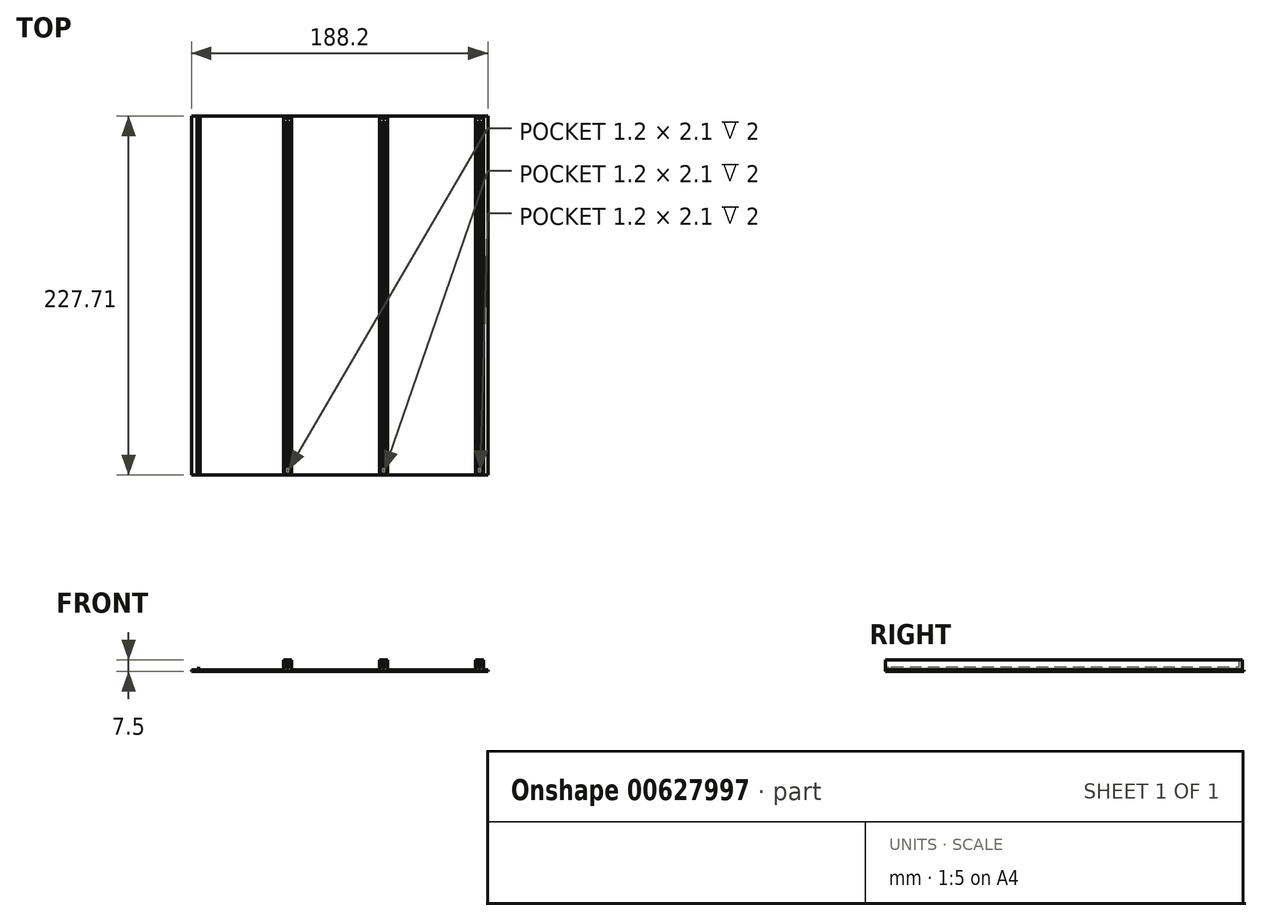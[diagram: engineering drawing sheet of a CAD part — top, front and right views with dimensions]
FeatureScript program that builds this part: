
annotation { "Feature Type Name" : "Feature", "Feature Type Description" : "" }
export const myFeature = defineFeature(function(context is Context, id is Id, definition is map)
    precondition{}
    {
        {
            var Q0;
            Q0=qCreatedBy(makeId("Top.planeOp"),FACE);
            var sketch = newSketch(context, id + "F0", { "sketchPlane" : qUnion([Q0])});
            skLineSegment(sketch, "E0.bottom", {"start": v(0, 0) * mm, "end": v(5.2, 0) * mm});
            skLineSegment(sketch, "E0.top", {"start": v(0, 226.71) * mm, "end": v(5.2, 226.71) * mm});
            skLineSegment(sketch, "E0.left", {"start": v(0, 0) * mm, "end": v(0, 226.71) * mm});
            skLineSegment(sketch, "E0.right", {"start": v(5.2, 0) * mm, "end": v(5.2, 226.71) * mm});
            skLineSegment(sketch, "E1.1.0.0", {"start": v(66.2, 0) * mm, "end": v(66.2, 226.71) * mm});
            skLineSegment(sketch, "E1.1.0.1", {"start": v(61, 0) * mm, "end": v(61, 226.71) * mm});
            skLineSegment(sketch, "E1.1.0.2", {"start": v(61, 226.71) * mm, "end": v(66.2, 226.71) * mm});
            skLineSegment(sketch, "E1.1.0.3", {"start": v(61, 0) * mm, "end": v(66.2, 0) * mm});
            skLineSegment(sketch, "E1.2.0.0", {"start": v(127.2, 0) * mm, "end": v(127.2, 226.71) * mm});
            skLineSegment(sketch, "E1.2.0.1", {"start": v(122, 0) * mm, "end": v(122, 226.71) * mm});
            skLineSegment(sketch, "E1.2.0.2", {"start": v(122, 226.71) * mm, "end": v(127.2, 226.71) * mm});
            skLineSegment(sketch, "E1.2.0.3", {"start": v(122, 0) * mm, "end": v(127.2, 0) * mm});
            skLineSegment(sketch, "E1.direction1", {"start": v(0, 0) * mm, "end": v(61, 0) * mm, "construction": true});
            skSolve(sketch);
        }
        {
            var Q0;
            Q0=makeQuery(id+"F0.imprint","IMPRINT",FACE,{"disambiguationData":[TD([[makeQuery(id+"F0.imprint","IMPRINT",EDGE,{"derivedFrom":sQuery(id+"F0.wireOp",EDGE,"E0.bottom")}),1.0]])]});
            var Q1;
            Q1=makeQuery(id+"F0.imprint","IMPRINT",FACE,{"disambiguationData":[TD([[makeQuery(id+"F0.imprint","IMPRINT",EDGE,{"derivedFrom":sQuery(id+"F0.wireOp",EDGE,"E1.1.0.0")}),1.0]])]});
            var Q2;
            Q2=makeQuery(id+"F0.imprint","IMPRINT",FACE,{"disambiguationData":[TD([[makeQuery(id+"F0.imprint","IMPRINT",EDGE,{"derivedFrom":sQuery(id+"F0.wireOp",EDGE,"E1.2.0.0")}),1.0]])]});
            extrude(context, id + "F1", {"entities" : qUnion([Q0, Q1, Q2]), "depth" : 2 * mm, "offsetDistance" : 25 * mm});
        }
        {
            var Q0;
            Q0=makeQuery(id+"F1.opExtrude","CAP_FACE",FACE,{"disambiguationData":[OSD([sQuery(id+"F0.wireOp",EDGE,"E0.bottom"),sQuery(id+"F0.wireOp",EDGE,"E0.top"),sQuery(id+"F0.wireOp",EDGE,"E0.left"),sQuery(id+"F0.wireOp",EDGE,"E0.right")])],"isStart":false});
            var sketch = newSketch(context, id + "F2", { "sketchPlane" : qUnion([Q0])});
            skLineSegment(sketch, "E2.bottom", {"start": v(0, 0) * mm, "end": v(2, 0) * mm});
            skLineSegment(sketch, "E2.top", {"start": v(0, 226.71) * mm, "end": v(5.2, 226.71) * mm});
            skLineSegment(sketch, "E2.left", {"start": v(0, 0) * mm, "end": v(0, 226.71) * mm});
            skLineSegment(sketch, "E2.right", {"start": v(5.2, 0) * mm, "end": v(5.2, 226.71) * mm});
            skLineSegment(sketch, "E3.top", {"start": v(2, 224.71) * mm, "end": v(3.2, 224.71) * mm});
            skLineSegment(sketch, "E3.left", {"start": v(2, 0) * mm, "end": v(2, 224.71) * mm});
            skLineSegment(sketch, "E3.right", {"start": v(3.2, 0) * mm, "end": v(3.2, 224.71) * mm});
            skLineSegment(sketch, "E4.trimOffspring", {"start": v(3.2, 0) * mm, "end": v(5.2, 0) * mm});
            skLineSegment(sketch, "E5.1.0.0", {"start": v(61, 0) * mm, "end": v(61, 226.71) * mm});
            skLineSegment(sketch, "E5.1.0.1", {"start": v(66.2, 0) * mm, "end": v(66.2, 226.71) * mm});
            skLineSegment(sketch, "E5.1.0.2", {"start": v(63, 0) * mm, "end": v(63, 224.71) * mm});
            skLineSegment(sketch, "E5.1.0.3", {"start": v(64.2, 0) * mm, "end": v(64.2, 224.71) * mm});
            skLineSegment(sketch, "E5.1.0.4", {"start": v(64.2, 0) * mm, "end": v(66.2, 0) * mm});
            skLineSegment(sketch, "E5.1.0.5", {"start": v(61, 226.71) * mm, "end": v(66.2, 226.71) * mm});
            skLineSegment(sketch, "E5.1.0.6", {"start": v(61, 0) * mm, "end": v(63, 0) * mm});
            skLineSegment(sketch, "E5.1.0.7", {"start": v(63, 224.71) * mm, "end": v(64.2, 224.71) * mm});
            skLineSegment(sketch, "E5.2.0.0", {"start": v(122, 0) * mm, "end": v(122, 226.71) * mm});
            skLineSegment(sketch, "E5.2.0.1", {"start": v(127.2, 0) * mm, "end": v(127.2, 226.71) * mm});
            skLineSegment(sketch, "E5.2.0.2", {"start": v(124, 0) * mm, "end": v(124, 224.71) * mm});
            skLineSegment(sketch, "E5.2.0.3", {"start": v(125.2, 0) * mm, "end": v(125.2, 224.71) * mm});
            skLineSegment(sketch, "E5.2.0.4", {"start": v(125.2, 0) * mm, "end": v(127.2, 0) * mm});
            skLineSegment(sketch, "E5.2.0.5", {"start": v(122, 226.71) * mm, "end": v(127.2, 226.71) * mm});
            skLineSegment(sketch, "E5.2.0.6", {"start": v(122, 0) * mm, "end": v(124, 0) * mm});
            skLineSegment(sketch, "E5.2.0.7", {"start": v(124, 224.71) * mm, "end": v(125.2, 224.71) * mm});
            skLineSegment(sketch, "E5.direction1", {"start": v(0, 0) * mm, "end": v(61, 0) * mm, "construction": true});
            skSolve(sketch);
        }
        {
            var Q0;
            Q0=makeQuery(id+"F2.imprint","IMPRINT",FACE,{"disambiguationData":[TD([[makeQuery(id+"F2.imprint","IMPRINT",EDGE,{"derivedFrom":sQuery(id+"F2.wireOp",EDGE,"E2.bottom")}),1.0]])]});
            var Q1;
            Q1=makeQuery(id+"F2.imprint","IMPRINT",FACE,{"disambiguationData":[TD([[makeQuery(id+"F2.imprint","IMPRINT",EDGE,{"derivedFrom":sQuery(id+"F2.wireOp",EDGE,"E5.1.0.0")}),-1.0]])]});
            var Q2;
            Q2=makeQuery(id+"F2.imprint","IMPRINT",FACE,{"disambiguationData":[TD([[makeQuery(id+"F2.imprint","IMPRINT",EDGE,{"derivedFrom":sQuery(id+"F2.wireOp",EDGE,"E5.2.0.0")}),-1.0]])]});
            extrude(context, id + "F3", {"entities" : qUnion([Q0, Q1, Q2]), "operationType" : NewBodyOperationType.ADD, "depth" : 4.5 * mm, "offsetDistance" : 25 * mm});
        }
        {
            var Q0;
            Q0=makeQuery(id+"F1.opExtrude","CAP_FACE",FACE,{"disambiguationData":[OSD([sQuery(id+"F0.wireOp",EDGE,"E0.bottom"),sQuery(id+"F0.wireOp",EDGE,"E0.top"),sQuery(id+"F0.wireOp",EDGE,"E0.left"),sQuery(id+"F0.wireOp",EDGE,"E0.right")])],"isStart":false});
            var sketch = newSketch(context, id + "F4", { "sketchPlane" : qUnion([Q0])});
            skLineSegment(sketch, "E6.bottom", {"start": v(2, 1.9) * mm, "end": v(3.2, 1.9) * mm});
            skLineSegment(sketch, "E6.top", {"start": v(2, 4) * mm, "end": v(3.2, 4) * mm});
            skLineSegment(sketch, "E6.left", {"start": v(2, 1.9) * mm, "end": v(2, 4) * mm});
            skLineSegment(sketch, "E6.right", {"start": v(3.2, 1.9) * mm, "end": v(3.2, 4) * mm});
            skLineSegment(sketch, "E7.1.0.0", {"start": v(63, 1.9) * mm, "end": v(64.2, 1.9) * mm});
            skLineSegment(sketch, "E7.1.0.1", {"start": v(63, 1.9) * mm, "end": v(63, 4) * mm});
            skLineSegment(sketch, "E7.1.0.2", {"start": v(63, 4) * mm, "end": v(64.2, 4) * mm});
            skLineSegment(sketch, "E7.1.0.3", {"start": v(64.2, 1.9) * mm, "end": v(64.2, 4) * mm});
            skLineSegment(sketch, "E7.2.0.0", {"start": v(124, 1.9) * mm, "end": v(125.2, 1.9) * mm});
            skLineSegment(sketch, "E7.2.0.1", {"start": v(124, 1.9) * mm, "end": v(124, 4) * mm});
            skLineSegment(sketch, "E7.2.0.2", {"start": v(124, 4) * mm, "end": v(125.2, 4) * mm});
            skLineSegment(sketch, "E7.2.0.3", {"start": v(125.2, 1.9) * mm, "end": v(125.2, 4) * mm});
            skLineSegment(sketch, "E7.direction1", {"start": v(2, 1.9) * mm, "end": v(63, 1.9) * mm, "construction": true});
            skSolve(sketch);
        }
        {
            var Q0;
            Q0=makeQuery(id+"F4.imprint","IMPRINT",FACE,{"disambiguationData":[TD([[makeQuery(id+"F4.imprint","IMPRINT",EDGE,{"derivedFrom":sQuery(id+"F4.wireOp",EDGE,"E6.bottom")}),1.0]])]});
            var Q1;
            Q1=makeQuery(id+"F4.imprint","IMPRINT",FACE,{"disambiguationData":[TD([[makeQuery(id+"F4.imprint","IMPRINT",EDGE,{"derivedFrom":sQuery(id+"F4.wireOp",EDGE,"E7.1.0.0")}),1.0]])]});
            var Q2;
            Q2=makeQuery(id+"F4.imprint","IMPRINT",FACE,{"disambiguationData":[TD([[makeQuery(id+"F4.imprint","IMPRINT",EDGE,{"derivedFrom":sQuery(id+"F4.wireOp",EDGE,"E7.2.0.0")}),1.0]])]});
            extrude(context, id + "F5", {"entities" : qUnion([Q0, Q1, Q2]), "operationType" : NewBodyOperationType.REMOVE, "oppositeDirection" : true, "depth" : 25 * mm, "offsetDistance" : 25 * mm});
        }
        {
            var Q0;
            Q0=qCreatedBy(makeId("Top.planeOp"),FACE);
            var sketch = newSketch(context, id + "F6", { "sketchPlane" : qUnion([Q0])});
            skLineSegment(sketch, "E8.top", {"start": v(-58.3, 227.71) * mm, "end": v(127.2, 227.71) * mm});
            skLineSegment(sketch, "E8.right", {"start": v(127.2, 0) * mm, "end": v(127.2, 227.71) * mm});
            skLineSegment(sketch, "E9", {"start": v(-58.3, 0) * mm, "end": v(127.2, 0) * mm});
            skLineSegment(sketch, "E10", {"start": v(-58.3, 0) * mm, "end": v(-58.3, 227.71) * mm});
            skLineSegment(sketch, "E11.bottom", {"start": v(127.2, 0) * mm, "end": v(129.9, 0) * mm});
            skLineSegment(sketch, "E11.top", {"start": v(127.2, 227.71) * mm, "end": v(129.9, 227.71) * mm});
            skLineSegment(sketch, "E11.right", {"start": v(129.9, 0) * mm, "end": v(129.9, 227.71) * mm});
            skSolve(sketch);
        }
        {
            var Q0;
            Q0=makeQuery(id+"F6.imprint","IMPRINT",FACE,{"disambiguationData":[TD([[makeQuery(id+"F6.imprint","IMPRINT",EDGE,{"derivedFrom":sQuery(id+"F6.wireOp",EDGE,"E8.top")}),-1.0]])]});
            var Q1;
            Q1=makeQuery(id+"F6.imprint","IMPRINT",FACE,{"disambiguationData":[TD([[makeQuery(id+"F6.imprint","IMPRINT",EDGE,{"derivedFrom":sQuery(id+"F6.wireOp",EDGE,"E11.bottom")}),1.0]])]});
            extrude(context, id + "F7", {"entities" : qUnion([Q0, Q1]), "operationType" : NewBodyOperationType.ADD, "oppositeDirection" : true, "depth" : 1 * mm, "offsetDistance" : 25 * mm});
        }
        {
            var Q0;
            {var subQ0=sQuery(id+"F6.wireOp",EDGE,"E8.bottom");var subQ1=sQuery(id+"F6.wireOp",EDGE,"E8.top");var subQ2=sQuery(id+"F6.wireOp",EDGE,"E8.left");var subQ3=sQuery(id+"F6.wireOp",EDGE,"E8.right");Q0=makeQuery(id+"F7.boolean.opBoolean","SPLIT",FACE,{"disambiguationData":[TD([makeQuery(id+"F1.opExtrude","SWEPT_FACE",FACE,{"disambiguationData":[OSD([sQuery(id+"F0.wireOp",EDGE,"E0.bottom")])]})])],"derivedFrom":makeQuery(id+"F7.opExtrude","CAP_FACE",FACE,{"disambiguationData":[OSD([subQ0,subQ1,subQ2,subQ3])],"isStart":true})});}
            var sketch = newSketch(context, id + "F8", { "sketchPlane" : qUnion([Q0])});
            skLineSegment(sketch, "E12.bottom", {"start": v(-52.8, 0) * mm, "end": v(-54.8, 0) * mm});
            skLineSegment(sketch, "E12.top", {"start": v(-52.8, 226.71) * mm, "end": v(-54.8, 226.71) * mm});
            skLineSegment(sketch, "E12.left", {"start": v(-52.8, 0) * mm, "end": v(-52.8, 226.71) * mm});
            skLineSegment(sketch, "E12.right", {"start": v(-54.8, 0) * mm, "end": v(-54.8, 226.71) * mm});
            skSolve(sketch);
        }
        {
            var Q0;
            Q0=makeQuery(id+"F8.imprint","IMPRINT",FACE,{"disambiguationData":[TD([[makeQuery(id+"F8.imprint","IMPRINT",EDGE,{"derivedFrom":sQuery(id+"F8.wireOp",EDGE,"E12.bottom")}),1.0]])]});
            extrude(context, id + "F9", {"entities" : qUnion([Q0]), "operationType" : NewBodyOperationType.ADD, "depth" : 1 * mm, "offsetDistance" : 25 * mm});
        }
        {
            var Q0;
            Q0=makeQuery(id+"F1.opExtrude","CAP_EDGE",EDGE,{"disambiguationData":[OSD([sQuery(id+"F0.wireOp",EDGE,"E0.bottom")])],"isStart":false});
            var Q1;
            Q1=makeQuery(id+"F1.opExtrude","CAP_EDGE",EDGE,{"disambiguationData":[OSD([sQuery(id+"F0.wireOp",EDGE,"E1.1.0.3")])],"isStart":false});
            var Q2;
            Q2=makeQuery(id+"F1.opExtrude","CAP_EDGE",EDGE,{"disambiguationData":[OSD([sQuery(id+"F0.wireOp",EDGE,"E1.2.0.3")])],"isStart":false});
            chamfer(context, id + "F10", {"entities" : qUnion([Q0, Q1, Q2]), "width" : 1 * mm, "tangentPropagation" : true});
        }
    });
